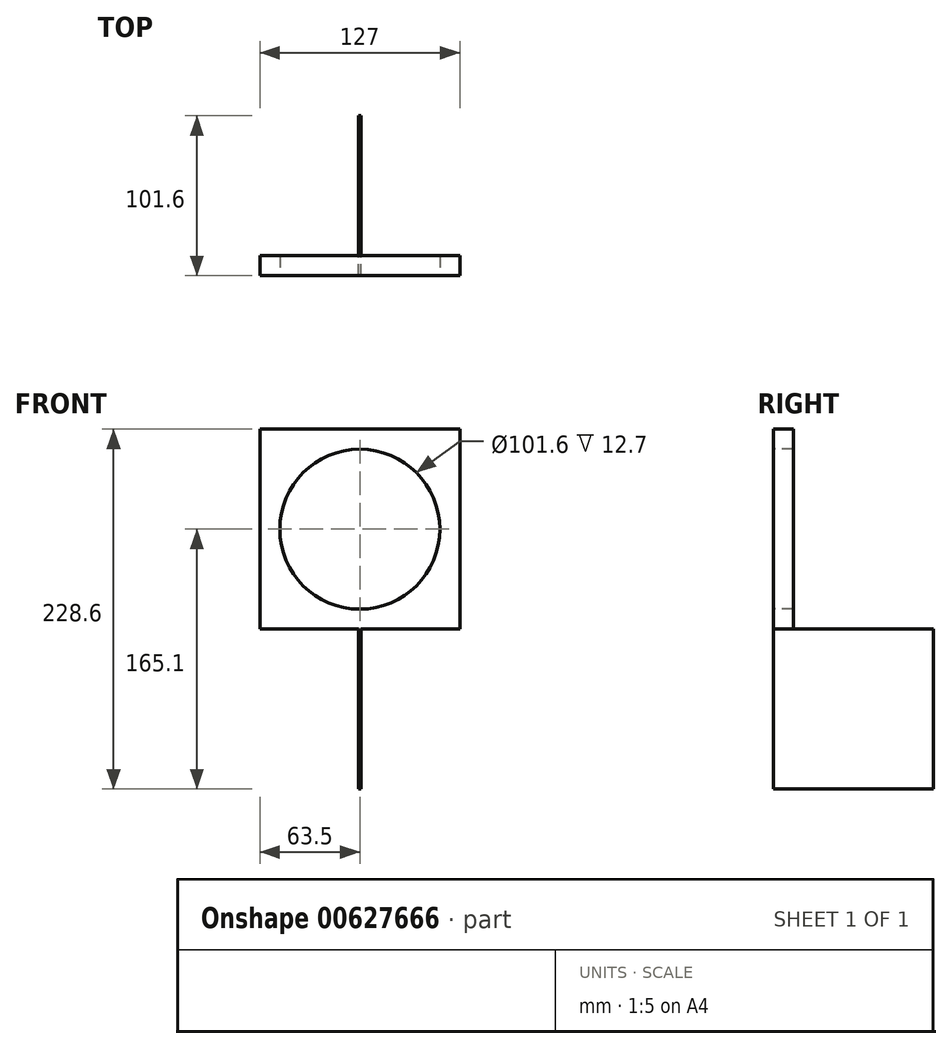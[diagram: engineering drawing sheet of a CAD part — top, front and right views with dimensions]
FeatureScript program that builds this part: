
annotation { "Feature Type Name" : "Feature", "Feature Type Description" : "" }
export const myFeature = defineFeature(function(context is Context, id is Id, definition is map)
    precondition{}
    {
        {
            var Q0;
            Q0=qCreatedBy(makeId("Front.planeOp"),FACE);
            var sketch = newSketch(context, id + "F0", { "sketchPlane" : qUnion([Q0])});
            skLineSegment(sketch, "E0.bottom", {"start": v(0, 0) * mm, "end": v(-127, 0) * mm});
            skLineSegment(sketch, "E0.top", {"start": v(0, 127) * mm, "end": v(-127, 127) * mm});
            skLineSegment(sketch, "E0.left", {"start": v(0, 0) * mm, "end": v(0, 127) * mm});
            skLineSegment(sketch, "E0.right", {"start": v(-127, 0) * mm, "end": v(-127, 127) * mm});
            skPoint(sketch, "E1", {"position": v(-63.5, 63.5) * mm});
            skPoint(sketch, "E1.positionSnap0", {"position": v(0, 63.5) * mm});
            skPoint(sketch, "E1.positionSnap1", {"position": v(-63.5, 0) * mm});
            skSolve(sketch);
        }
        {
            var Q0;
            Q0=makeQuery(id+"F0.imprint","IMPRINT",FACE,{"disambiguationData":[TD([[makeQuery(id+"F0.imprint","IMPRINT",EDGE,{"derivedFrom":sQuery(id+"F0.wireOp",EDGE,"E0.bottom")}),-1.0]])]});
            extrude(context, id + "F1", {"entities" : qUnion([Q0]), "depth" : 12.7 * mm, "offsetDistance" : 25.4 * mm});
        }
        {
            var Q0;
            Q0=makeQuery(id+"F1.opExtrude","CAP_FACE",FACE,{"disambiguationData":[OSD([sQuery(id+"F0.wireOp",EDGE,"E0.bottom"),sQuery(id+"F0.wireOp",EDGE,"E0.top"),sQuery(id+"F0.wireOp",EDGE,"E0.left"),sQuery(id+"F0.wireOp",EDGE,"E0.right")])],"isStart":false});
            var sketch = newSketch(context, id + "F2", { "sketchPlane" : qUnion([Q0])});
            skPoint(sketch, "E2", {"position": v(-63.5, 63.5) * mm});
            skPoint(sketch, "E2.positionSnap0", {"position": v(0, 63.5) * mm});
            skPoint(sketch, "E2.positionSnap1", {"position": v(-63.5, 0) * mm});
            skSolve(sketch);
        }
        {
            var Q0;
            Q0=sQuery(id+"F2.wireOp",VERTEX,"E2");
            var Q1;
            Q1=makeQuery(id+"F1.opExtrude","SWEPT_BODY",BODY,{"disambiguationData":[OSD([sQuery(id+"F0.wireOp",EDGE,"E0.bottom"),sQuery(id+"F0.wireOp",EDGE,"E0.top"),sQuery(id+"F0.wireOp",EDGE,"E0.left"),sQuery(id+"F0.wireOp",EDGE,"E0.right")])]});
            hole(context, id + "F3", {"style" : HoleStyle.SIMPLE, "endStyle" : HoleEndStyle.THROUGH, "holeDiameter" : 101.6 * mm, "majorDiameter" : 6.35 * mm, "isTappedThrough" : true, "tappedDepth" : 12.7 * mm, "tapClearance" : 3, "locations" : qUnion([Q0]), "scope" : qUnion([Q1])});
        }
        {
            var Q0;
            Q0=makeQuery(id+"F1.opExtrude","SWEPT_FACE",FACE,{"disambiguationData":[OSD([sQuery(id+"F0.wireOp",EDGE,"E0.bottom")])]});
            var sketch = newSketch(context, id + "F4", { "sketchPlane" : qUnion([Q0])});
            skPoint(sketch, "E3.positionSnap0", {"position": v(-63.5, 0) * mm});
            skPoint(sketch, "E4", {"position": v(-63.5, -38.1) * mm});
            skPoint(sketch, "E4.positionSnap0", {"position": v(-63.5, 12.7) * mm});
            skLineSegment(sketch, "E5.bottom", {"start": v(-64.3, 12.7) * mm, "end": v(-62.7, 12.7) * mm});
            skLineSegment(sketch, "E5.top", {"start": v(-64.3, -88.9) * mm, "end": v(-62.7, -88.9) * mm});
            skLineSegment(sketch, "E5.left", {"start": v(-64.3, 12.7) * mm, "end": v(-64.3, -88.9) * mm});
            skLineSegment(sketch, "E5.right", {"start": v(-62.7, 12.7) * mm, "end": v(-62.7, -88.9) * mm});
            skSolve(sketch);
        }
        {
            var Q0;
            {var subQ0=sQuery(id+"F4.wireOp",EDGE,"E5.top");Q0=makeQuery(id+"F4.imprint","IMPRINT",FACE,{"disambiguationData":[TD([[makeQuery(id+"F4.imprint","IMPRINT",EDGE,{"derivedFrom":subQ0}),1.0]])]});}
            var Q1;
            {var subQ0=sQuery(id+"F4.wireOp",EDGE,"E5.bottom");Q1=makeQuery(id+"F4.imprint","IMPRINT",FACE,{"disambiguationData":[TD([[makeQuery(id+"F4.imprint","IMPRINT",EDGE,{"derivedFrom":subQ0}),1.0]])]});}
            extrude(context, id + "F5", {"entities" : qUnion([Q0, Q1]), "operationType" : NewBodyOperationType.ADD, "depth" : 101.6 * mm, "offsetDistance" : 25.4 * mm});
        }
    });
